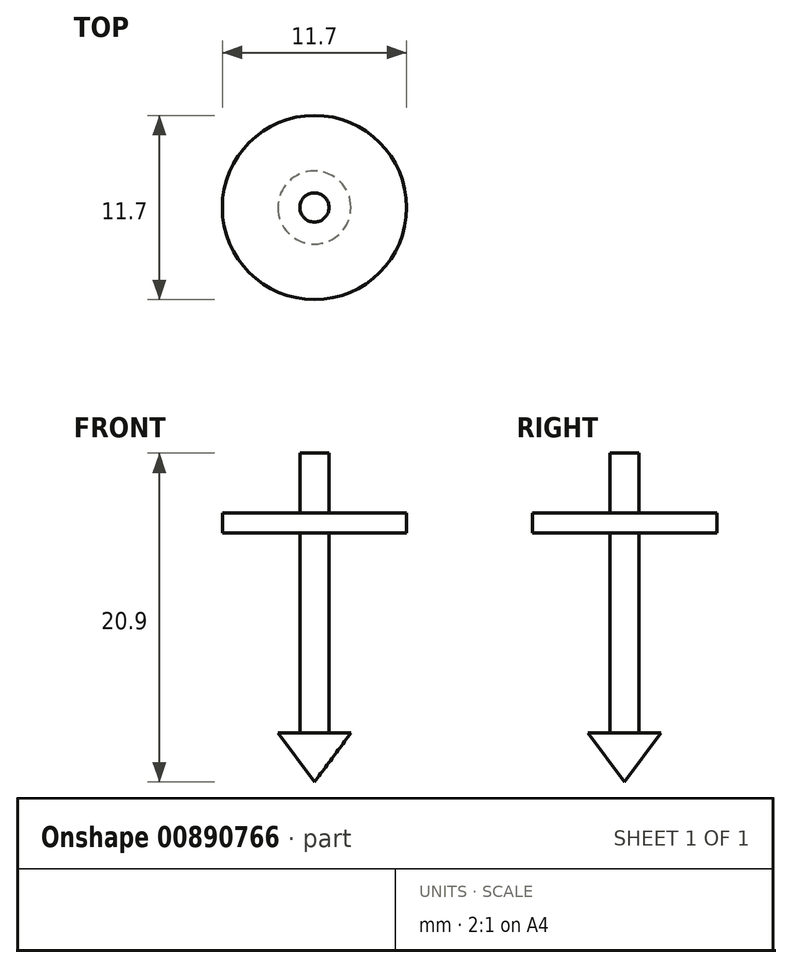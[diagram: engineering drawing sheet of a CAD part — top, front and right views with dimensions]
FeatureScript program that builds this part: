
annotation { "Feature Type Name" : "Feature", "Feature Type Description" : "" }
export const myFeature = defineFeature(function(context is Context, id is Id, definition is map)
    precondition{}
    {
        {
            var Q0;
            Q0=qCreatedBy(makeId("Top.planeOp"),FACE);
            var sketch = newSketch(context, id + "F0", { "sketchPlane" : qUnion([Q0])});
            skCircle(sketch, "E0", {"center": v(0, 0) * mm, "radius": 0.93 * mm});
            skCircle(sketch, "E1", {"center": v(0, 0) * mm, "radius": 3.8 * mm});
            skSolve(sketch);
        }
        {
            var Q0;
            Q0=makeQuery(id+"F0.imprint","IMPRINT",FACE,{"disambiguationData":[TD([[makeQuery(id+"F0.imprint","IMPRINT",EDGE,{"derivedFrom":sQuery(id+"F0.wireOp",EDGE,"E0")}),1.0]])]});
            extrude(context, id + "F1", {"entities" : qUnion([Q0]), "endBound" : BoundingType.SYMMETRIC, "depth" : 25.4 * mm, "offsetDistance" : 25.4 * mm});
        }
        {
            var Q0;
            Q0=qCreatedBy(makeId("Front.planeOp"),FACE);
            var sketch = newSketch(context, id + "F2", { "sketchPlane" : qUnion([Q0])});
            skLineSegment(sketch, "E2", {"start": v(0, 0) * mm, "end": v(0, -12.7) * mm});
            skLineSegment(sketch, "E3", {"start": v(0, -12.7) * mm, "end": v(-2.32, -12.7) * mm});
            skLineSegment(sketch, "E4", {"start": v(-2.32, -12.7) * mm, "end": v(0, -15.82) * mm});
            skLineSegment(sketch, "E5", {"start": v(0, -15.82) * mm, "end": v(0, -12.7) * mm});
            skSolve(sketch);
        }
        {
            var Q0;
            Q0=makeQuery(id+"F2.imprint","IMPRINT",FACE,{"disambiguationData":[TD([[makeQuery(id+"F2.imprint","IMPRINT",EDGE,{"derivedFrom":sQuery(id+"F2.wireOp",EDGE,"E3")}),1.0]])]});
            var Q1;
            Q1=sQuery(id+"F2.wireOp",EDGE,"E5");
            revolve(context, id + "F3", {"operationType" : NewBodyOperationType.ADD, "surfaceOperationType" : NewSurfaceOperationType.NEW, "entities" : qUnion([Q0]), "axis" : qUnion([Q1]), "revolveType" : RevolveType.FULL});
        }
        {
            var Q0;
            Q0=makeQuery(id+"F1.opExtrude","CAP_FACE",FACE,{"disambiguationData":[OSD([sQuery(id+"F0.wireOp",EDGE,"E0")])],"isStart":false});
            extrude(context, id + "F4", {"entities" : qUnion([Q0]), "operationType" : NewBodyOperationType.REMOVE, "oppositeDirection" : true, "depth" : 7.62 * mm, "offsetDistance" : 25.4 * mm});
        }
        {
            var Q0;
            Q0=qCreatedBy(makeId("Top.planeOp"),FACE);
            var sketch = newSketch(context, id + "F5", { "sketchPlane" : qUnion([Q0])});
            skCircle(sketch, "E6", {"center": v(0, 0) * mm, "radius": 5.85 * mm});
            skSolve(sketch);
        }
        {
            var Q0;
            Q0=makeQuery(id+"F5.imprint","IMPRINT",FACE,{"disambiguationData":[TD([[makeQuery(id+"F5.imprint","IMPRINT",EDGE,{"derivedFrom":sQuery(id+"F5.wireOp",EDGE,"E6")}),1.0]])]});
            extrude(context, id + "F6", {"entities" : qUnion([Q0]), "operationType" : NewBodyOperationType.ADD, "depth" : 1.27 * mm, "offsetDistance" : 25.4 * mm});
        }
    });
